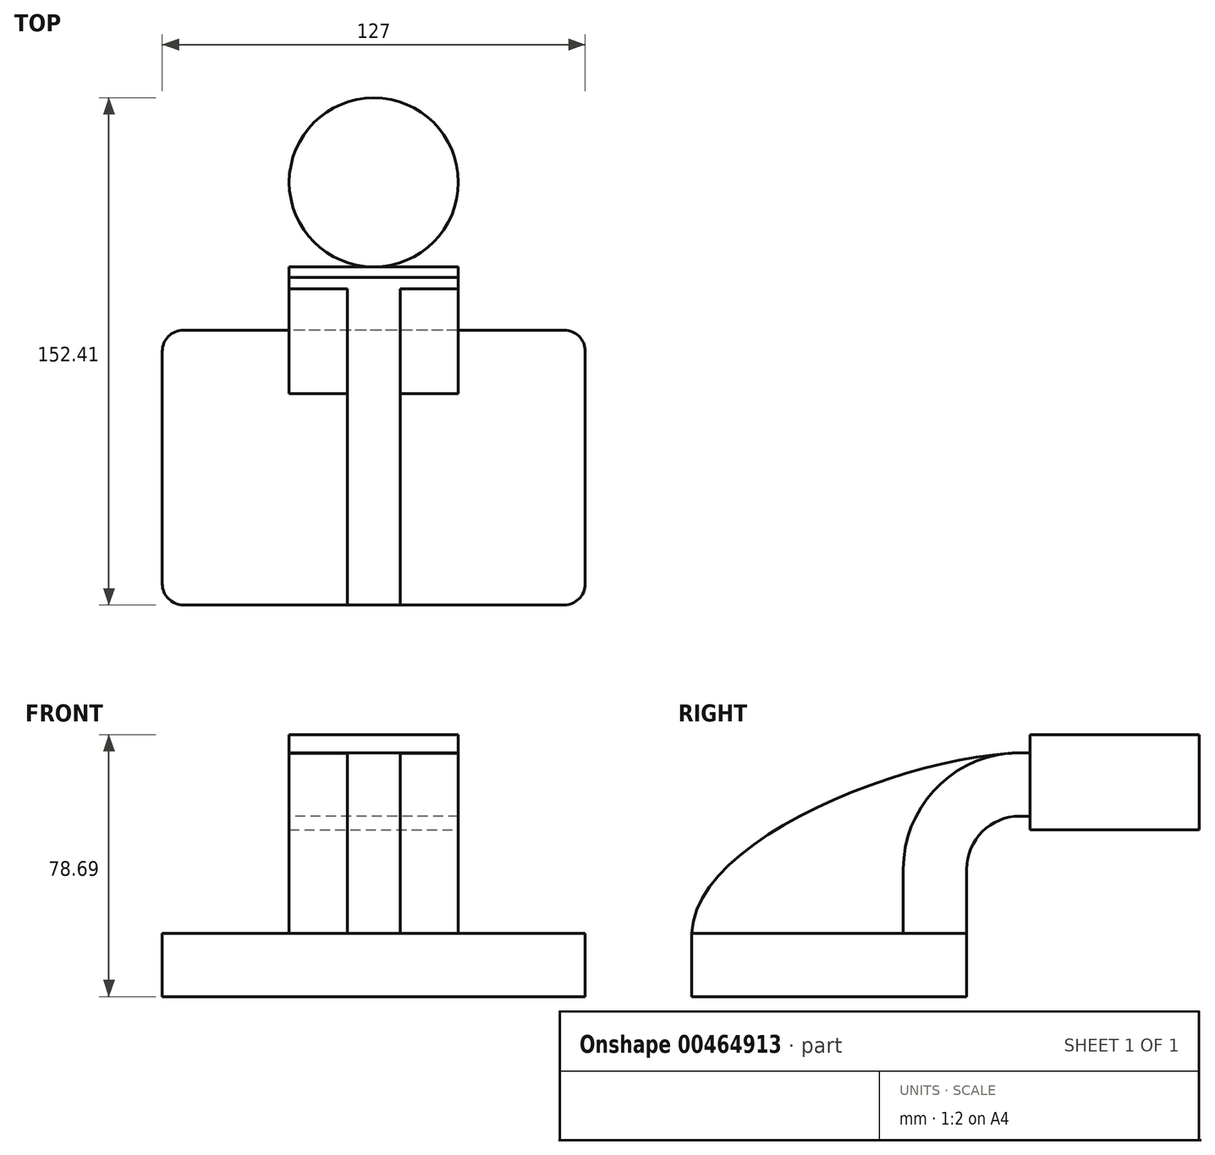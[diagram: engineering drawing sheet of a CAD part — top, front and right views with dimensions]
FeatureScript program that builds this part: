
annotation { "Feature Type Name" : "Feature", "Feature Type Description" : "" }
export const myFeature = defineFeature(function(context is Context, id is Id, definition is map)
    precondition{}
    {
        {
            var Q0;
            Q0=qCreatedBy(makeId("Right.planeOp"),FACE);
            var sketch = newSketch(context, id + "F0", { "sketchPlane" : qUnion([Q0])});
            skLineSegment(sketch, "E0.bottom", {"start": v(-41.28, 9.52) * mm, "end": v(41.27, 9.53) * mm});
            skLineSegment(sketch, "E0.top", {"start": v(-41.28, -9.52) * mm, "end": v(41.28, -9.52) * mm});
            skLineSegment(sketch, "E0.left", {"start": v(-41.28, 9.52) * mm, "end": v(-41.28, -9.53) * mm});
            skLineSegment(sketch, "E0.right", {"start": v(41.27, 9.53) * mm, "end": v(41.28, -9.52) * mm});
            skPoint(sketch, "E0.middle", {"position": v(0, 0) * mm});
            skPoint(sketch, "E1.middle", {"position": v(85.72, 116.48) * mm});
            skLineSegment(sketch, "E2.bottom", {"start": v(60.32, 40.59) * mm, "end": v(111.12, 40.59) * mm});
            skLineSegment(sketch, "E2.top", {"start": v(60.32, 69.16) * mm, "end": v(111.12, 69.16) * mm});
            skLineSegment(sketch, "E2.left", {"start": v(60.32, 40.59) * mm, "end": v(60.32, 69.16) * mm});
            skLineSegment(sketch, "E2.right", {"start": v(111.12, 40.59) * mm, "end": v(111.12, 69.16) * mm});
            skPoint(sketch, "E2.middle", {"position": v(85.73, 54.88) * mm});
            skLineSegment(sketch, "E3", {"start": v(41.27, 9.53) * mm, "end": v(41.27, 28.8) * mm});
            skArc(sketch, "E4", {"start": v(41.27, 28.8) * mm, "mid": v(45.92, 40.03) * mm, "end": v(57.15, 44.68) * mm});
            skLineSegment(sketch, "E5", {"start": v(57.15, 44.68) * mm, "end": v(85.3, 44.68) * mm});
            skLineSegment(sketch, "E6.0", {"start": v(57.15, 63.73) * mm, "end": v(85.3, 63.73) * mm});
            skArc(sketch, "E6.1", {"start": v(22.22, 28.8) * mm, "mid": v(32.45, 53.5) * mm, "end": v(57.15, 63.73) * mm});
            skLineSegment(sketch, "E6.2", {"start": v(22.22, 9.53) * mm, "end": v(22.22, 28.8) * mm});
            skLineSegment(sketch, "E7", {"start": v(85.72, 40.59) * mm, "end": v(85.72, 69.16) * mm});
            skFitSpline(sketch, "E8", {"points": [v(-41.28, 9.53) * mm, v(57.15, 63.73) * mm], "startDerivative": vector(2, 85.19) * mm, "endDerivative": vector(100.82, 2.8) * mm});
            skSolve(sketch);
        }
        {
            var Q0;
            {var subQ1=sQuery(id+"F0.wireOp",EDGE,"E3");Q0=makeQuery(id+"F0.imprint","IMPRINT",FACE,{"disambiguationData":[TD([[makeQuery(id+"F0.imprint","IMPRINT",EDGE,{"derivedFrom":subQ1}),1.0]])]});}
            extrude(context, id + "F1", {"entities" : qUnion([Q0]), "endBound" : BoundingType.SYMMETRIC, "depth" : 50.8 * mm});
        }
        {
            var Q0;
            Q0=makeQuery(id+"F0.imprint","IMPRINT",FACE,{"disambiguationData":[TD([[makeQuery(id+"F0.imprint","IMPRINT",EDGE,{"derivedFrom":sQuery(id+"F0.wireOp",EDGE,"E0.top")}),1.0]])]});
            extrude(context, id + "F2", {"entities" : qUnion([Q0]), "operationType" : NewBodyOperationType.ADD, "endBound" : BoundingType.SYMMETRIC, "depth" : 127 * mm});
        }
        {
            var Q0;
            {var subQ3=sQuery(id+"F0.wireOp",EDGE,"E6.2");Q0=makeQuery(id+"F0.imprint","IMPRINT",FACE,{"disambiguationData":[TD([[makeQuery(id+"F0.imprint","IMPRINT",EDGE,{"derivedFrom":subQ3}),1.0]])]});}
            extrude(context, id + "F3", {"entities" : qUnion([Q0]), "operationType" : NewBodyOperationType.ADD, "endBound" : BoundingType.SYMMETRIC, "depth" : 15.88 * mm});
        }
        {
            var Q0;
            {var subQ0=sQuery(id+"F0.wireOp",EDGE,"E2.right");Q0=makeQuery(id+"F0.imprint","IMPRINT",FACE,{"disambiguationData":[TD([[makeQuery(id+"F0.imprint","IMPRINT",EDGE,{"derivedFrom":subQ0}),1.0]])]});}
            var Q1;
            Q1=sQuery(id+"F0.wireOp",EDGE,"E7");
            revolve(context, id + "F4", {"operationType" : NewBodyOperationType.ADD, "entities" : qUnion([Q0]), "axis" : qUnion([Q1]), "revolveType" : RevolveType.FULL});
        }
        {
            var Q0;
            Q0=makeQuery(id+"F2.opExtrude","CAP_EDGE",EDGE,{"disambiguationData":[OSD([sQuery(id+"F0.wireOp",EDGE,"E0.left")])],"isStart":false});
            var Q1;
            Q1=makeQuery(id+"F2.opExtrude","CAP_EDGE",EDGE,{"disambiguationData":[OSD([sQuery(id+"F0.wireOp",EDGE,"E0.right")])],"isStart":false});
            var Q2;
            Q2=makeQuery(id+"F2.opExtrude","CAP_EDGE",EDGE,{"disambiguationData":[OSD([sQuery(id+"F0.wireOp",EDGE,"E0.right")])],"isStart":true});
            var Q3;
            Q3=makeQuery(id+"F2.opExtrude","CAP_EDGE",EDGE,{"disambiguationData":[OSD([sQuery(id+"F0.wireOp",EDGE,"E0.left")])],"isStart":true});
            fillet(context, id + "F5", {"entities" : qUnion([Q0, Q1, Q2, Q3]), "radius" : 6.35 * mm, "tangentPropagation" : true, "allowEdgeOverflow" : false});
        }
    });
